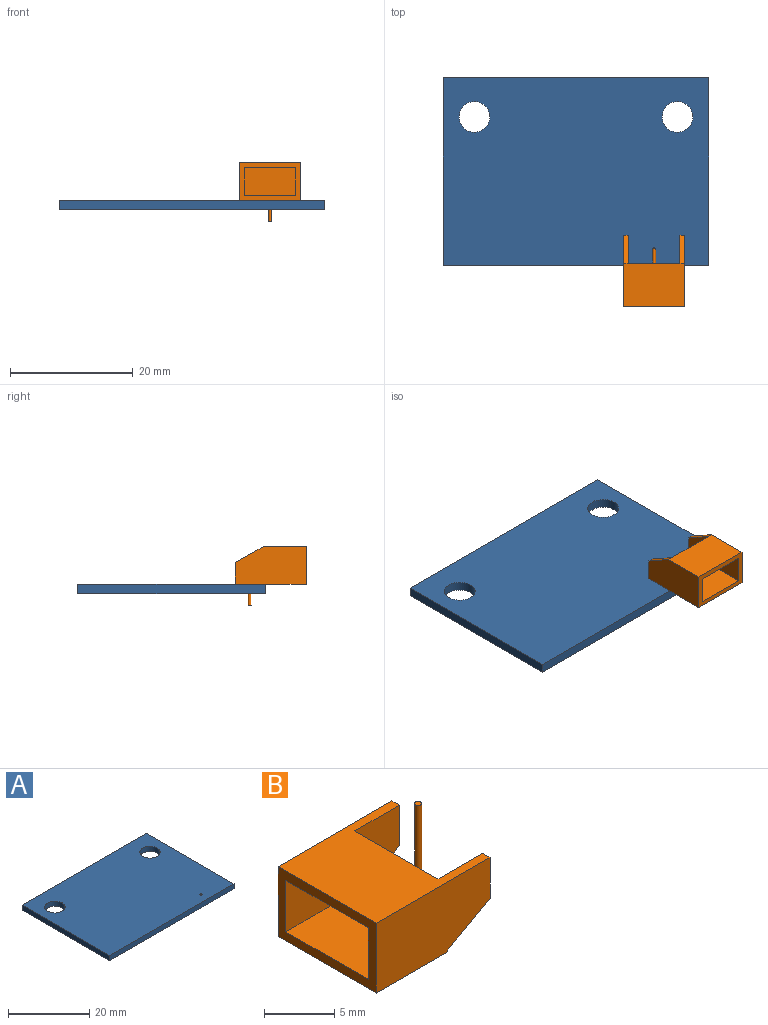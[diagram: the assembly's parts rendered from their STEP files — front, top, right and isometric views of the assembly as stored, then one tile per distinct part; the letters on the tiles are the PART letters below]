
ASSEMBLY  parts=2 mates=1
PART A: 9 faces, bbox 43.2x30.5x1.5 mm
  f0: plane 30.48x1.52mm, normal (-1,0,0), area 46.5mm2, adj f1,f4,f6,f7
  f1: plane 43.18x1.52mm, normal (0,-1,0), area 65.8mm2, adj f0,f2,f6,f7
  f2: plane 30.48x1.52mm, normal (1,0,0), area 46.5mm2, adj f1,f4,f6,f7
  f3: cylinder r=2.5mm len=5mm, axis (0,0,-1), area 23.9mm2, adj f6,f7
  f4: plane 43.18x1.52mm, normal (0,1,0), area 65.8mm2, adj f0,f2,f6,f7
  f5: cylinder r=2.5mm len=5mm, axis (0,0,-1), area 23.9mm2, adj f6,f7
  f6: plane 43.18x30.48mm, normal (0,0,1), area 1276.6mm2, adj f0,f1,f2,f3,f4,f5,f8
  f7: plane 43.18x30.48mm, normal (0,0,-1), area 1276.6mm2, adj f0,f1,f2,f3,f4,f5,f8
  f8: cylinder r=0.28mm len=1.52mm, axis (0,0,1), area 2.7mm2, adj f6,f7
PART B: 20 faces, bbox 11.5x9.9x9.5 mm
  f0: plane 9.9x6.1mm, normal (-1,0,0), area 23mm2, adj f3,f4,f5,f6,f15,f16,f17,f18
  f1: plane 3.56x0.75mm, normal (1,0,0), area 2.7mm2, adj f4,f6,f9,f13
  f2: plane 3.56x0.75mm, normal (1,0,0), area 2.7mm2, adj f4,f5,f7,f14
  f3: plane 9.9x7mm, normal (0,0,-1), area 69.3mm2, adj f0,f5,f6,f8,f13,f14
  f4: plane 11.5x9.9mm, normal (0,0,1), area 76.1mm2, adj f0,f1,f2,f5,f6,f7,f8,f9
  f5: plane 11.5x6.1mm, normal (0,1,0), area 64.4mm2, adj f0,f2,f3,f4,f14
  f6: plane 11.5x6.1mm, normal (0,-1,0), area 64.4mm2, adj f0,f1,f3,f4,f13
  f7: plane 6.1x4.5mm, normal (0,-1,0), area 21.7mm2, adj f2,f4,f8,f14
  f8: plane 8.4x6.1mm, normal (1,0,0), area 51mm2, adj f3,f4,f7,f9,f11
  f9: plane 6.1x4.5mm, normal (0,1,0), area 21.7mm2, adj f1,f4,f8,f13
  f10: plane 0.5x0.5mm, normal (0,0,1), area 0.2mm2, adj f12
  f11: cylinder r=0.25mm len=2.45mm, axis (-1,0,0), area 3.5mm2, adj f8,f12
  f12: cylinder r=0.25mm len=6.35mm, axis (0,0,-1), area 9.6mm2, adj f10,f11
  f13: plane 4.5x2.54mm, normal (0.49,0,-0.87), area 3.9mm2, adj f1,f3,f6,f9
  f14: plane 4.5x2.54mm, normal (0.49,0,-0.87), area 3.9mm2, adj f2,f3,f5,f7
  f15: plane 8.3x4.95mm, normal (0,0,-1), area 41.1mm2, adj f0,f16,f18,f19
  f16: plane 4.95x4.5mm, normal (0,-1,0), area 22.3mm2, adj f0,f15,f17,f19
  f17: plane 8.3x4.95mm, normal (0,0,1), area 41.1mm2, adj f0,f16,f18,f19
  f18: plane 4.95x4.5mm, normal (0,1,0), area 22.3mm2, adj f0,f15,f17,f19
  f19: plane 8.3x4.5mm, normal (-1,0,0), area 37.4mm2, adj f15,f16,f17,f18
PLACE A t=(-9.62,-7.81,0.87)mm
PLACE B rot(axis=(0.71,0.71,0),180deg) t=(24.67,-14.47,8.49)mm
MATE fastened B.f12 <-> A.f8  axis (0,0,-1) through (24.67,-5.27,-1.01)mm
